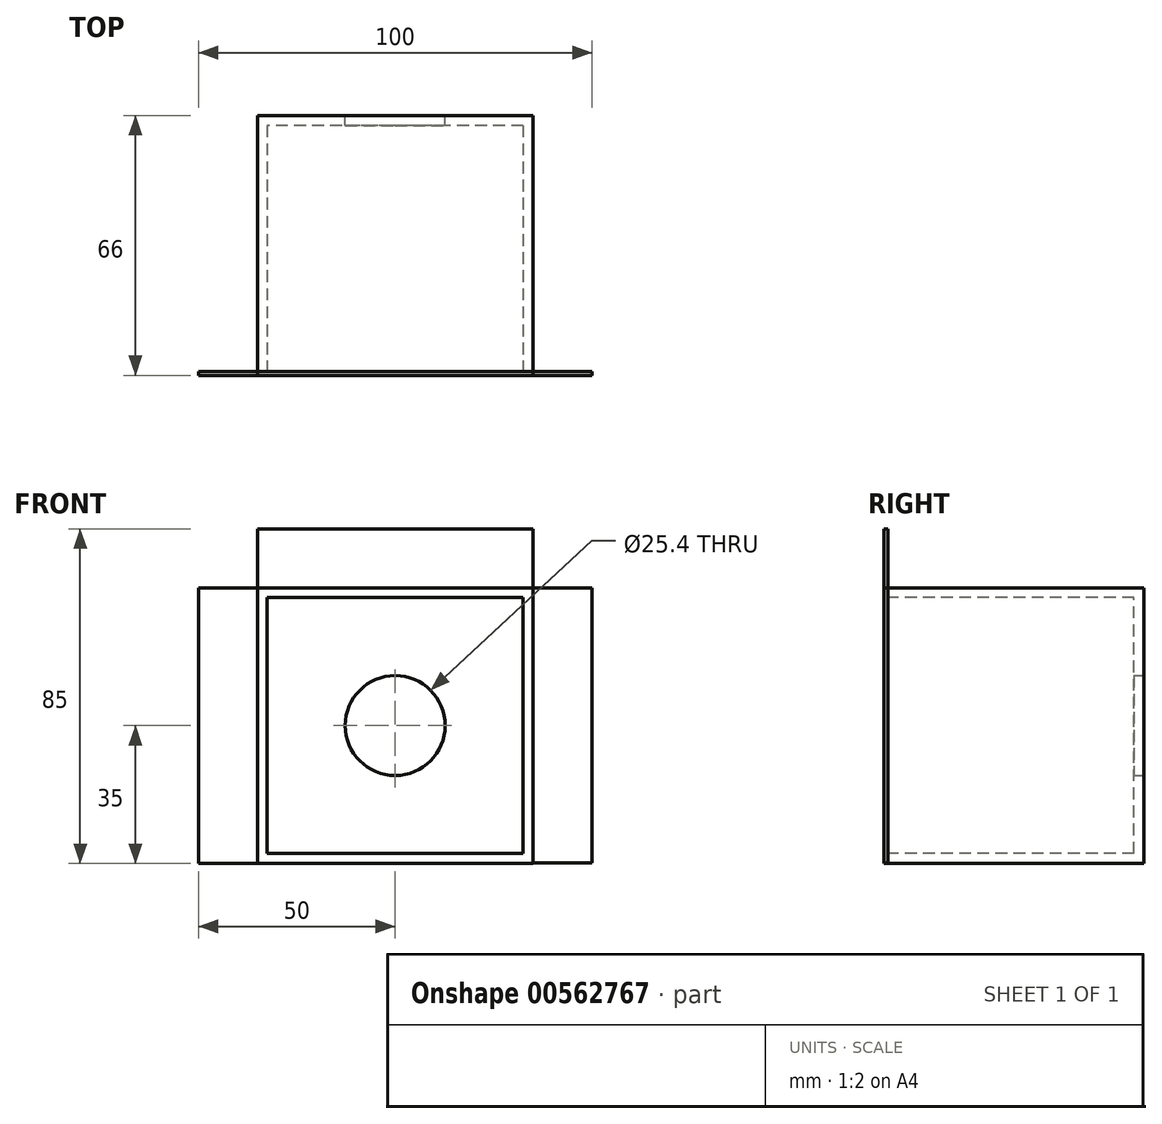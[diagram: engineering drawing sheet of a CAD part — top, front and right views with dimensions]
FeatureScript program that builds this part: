
annotation { "Feature Type Name" : "Feature", "Feature Type Description" : "" }
export const myFeature = defineFeature(function(context is Context, id is Id, definition is map)
    precondition{}
    {
        {
            var Q0;
            Q0=qCreatedBy(makeId("Front.planeOp"),FACE);
            var sketch = newSketch(context, id + "F0", { "sketchPlane" : qUnion([Q0])});
            skLineSegment(sketch, "E0.bottom", {"start": v(35, -35) * mm, "end": v(-35, -35) * mm});
            skLineSegment(sketch, "E0.top", {"start": v(35, 35) * mm, "end": v(-35, 35) * mm});
            skLineSegment(sketch, "E0.left", {"start": v(35, -35) * mm, "end": v(35, 35) * mm});
            skLineSegment(sketch, "E0.right", {"start": v(-35, -35) * mm, "end": v(-35, 35) * mm});
            skPoint(sketch, "E0.middle", {"position": v(0, 0) * mm});
            skLineSegment(sketch, "E1.bottom", {"start": v(35, 35) * mm, "end": v(50, 35) * mm});
            skLineSegment(sketch, "E1.top", {"start": v(35, -34.88) * mm, "end": v(50, -34.88) * mm});
            skLineSegment(sketch, "E1.left", {"start": v(35, 35) * mm, "end": v(35, -34.88) * mm});
            skLineSegment(sketch, "E1.right", {"start": v(50, 35) * mm, "end": v(50, -34.88) * mm});
            skLineSegment(sketch, "E2.top", {"start": v(35, 50) * mm, "end": v(-35, 50) * mm});
            skLineSegment(sketch, "E2.left", {"start": v(35, 35) * mm, "end": v(35, 50) * mm});
            skLineSegment(sketch, "E2.right", {"start": v(-35, 35) * mm, "end": v(-35, 50) * mm});
            skLineSegment(sketch, "E3.bottom", {"start": v(-35, 35) * mm, "end": v(-50, 35) * mm});
            skLineSegment(sketch, "E3.top", {"start": v(-35, -35) * mm, "end": v(-50, -35) * mm});
            skLineSegment(sketch, "E3.left", {"start": v(-35, 35) * mm, "end": v(-35, -35) * mm});
            skLineSegment(sketch, "E3.right", {"start": v(-50, 35) * mm, "end": v(-50, -35) * mm});
            skLineSegment(sketch, "E4.bottom", {"start": v(-35, -35) * mm, "end": v(35, -35) * mm});
            skLineSegment(sketch, "E4.top", {"start": v(-35, -50) * mm, "end": v(35, -50) * mm});
            skLineSegment(sketch, "E4.left", {"start": v(-35, -35) * mm, "end": v(-35, -50) * mm});
            skLineSegment(sketch, "E4.right", {"start": v(35, -35) * mm, "end": v(35, -50) * mm});
            skSolve(sketch);
        }
        {
            var Q0;
            Q0=qCreatedBy(makeId("Front.planeOp"),FACE);
            cPlane(context, id + "F1", {"entities" : qUnion([Q0]), "cplaneType" : CPlaneType.OFFSET, "offset" : 65 * mm, "oppositeDirection" : true, "width" : 150 * mm, "height" : 150 * mm});
        }
        {
            var Q0;
            Q0=qCreatedBy(id+"F1.planeOp",FACE);
            var sketch = newSketch(context, id + "F2", { "sketchPlane" : qUnion([Q0])});
            skLineSegment(sketch, "E5.bottom", {"start": v(35, 35) * mm, "end": v(-35, 35) * mm});
            skLineSegment(sketch, "E5.top", {"start": v(35, -35) * mm, "end": v(-35, -35) * mm});
            skLineSegment(sketch, "E5.left", {"start": v(35, 35) * mm, "end": v(35, -35) * mm});
            skLineSegment(sketch, "E5.right", {"start": v(-35, 35) * mm, "end": v(-35, -35) * mm});
            skPoint(sketch, "E5.middle", {"position": v(0, 0) * mm});
            skSolve(sketch);
        }
        {
            var Q0;
            Q0=makeQuery(id+"F0.imprint","IMPRINT",FACE,{"disambiguationData":[TD([[makeQuery(id+"F0.imprint","IMPRINT",EDGE,{"derivedFrom":sQuery(id+"F0.wireOp",EDGE,"E0.left")}),1.0]])]});
            var Q1;
            Q1=sQuery(id+"F2.wireOp",VERTEX,"E5.middle");
            extrude(context, id + "F3", {"entities" : qUnion([Q0]), "endBound" : BoundingType.UP_TO_VERTEX, "oppositeDirection" : true, "depth" : 25 * mm, "endBoundEntityVertex" : qUnion([Q1]), "offsetDistance" : 25 * mm});
        }
        {
            var Q0;
            Q0=makeQuery(id+"F0.imprint","IMPRINT",FACE,{"disambiguationData":[TD([[makeQuery(id+"F0.imprint","IMPRINT",EDGE,{"derivedFrom":sQuery(id+"F0.wireOp",EDGE,"E3.bottom")}),1.0]])]});
            var Q1;
            Q1=makeQuery(id+"F0.imprint","IMPRINT",FACE,{"disambiguationData":[TD([[makeQuery(id+"F0.imprint","IMPRINT",EDGE,{"derivedFrom":sQuery(id+"F0.wireOp",EDGE,"E0.top")}),-1.0]])]});
            var Q2;
            Q2=makeQuery(id+"F0.imprint","IMPRINT",FACE,{"disambiguationData":[TD([[makeQuery(id+"F0.imprint","IMPRINT",EDGE,{"derivedFrom":sQuery(id+"F0.wireOp",EDGE,"E1.bottom")}),-1.0]])]});
            var Q3;
            Q3=makeQuery(id+"F0.imprint","IMPRINT",FACE,{"disambiguationData":[TD([[makeQuery(id+"F0.imprint","IMPRINT",EDGE,{"derivedFrom":sQuery(id+"F0.wireOp",EDGE,"E4.bottom")}),-1.0]])]});
            extrude(context, id + "F4", {"entities" : qUnion([Q0, Q1, Q2, Q3]), "depth" : 1 * mm, "offsetDistance" : 25 * mm});
        }
        {
            var Q0;
            Q0=makeQuery(id+"F3.opExtrude","CAP_FACE",FACE,{"disambiguationData":[OSD([sQuery(id+"F0.wireOp",EDGE,"E0.left"),sQuery(id+"F0.wireOp",EDGE,"E1.left"),sQuery(id+"F0.wireOp",EDGE,"E0.top"),sQuery(id+"F0.wireOp",EDGE,"E3.left"),sQuery(id+"F0.wireOp",EDGE,"E4.bottom")])],"isStart":true});
            var Q1;
            Q1=makeQuery(id+"F3.opExtrude","SWEPT_BODY",BODY,{"disambiguationData":[OSD([sQuery(id+"F0.wireOp",EDGE,"E0.left"),sQuery(id+"F0.wireOp",EDGE,"E1.left"),sQuery(id+"F0.wireOp",EDGE,"E0.top"),sQuery(id+"F0.wireOp",EDGE,"E3.left"),sQuery(id+"F0.wireOp",EDGE,"E4.bottom")])]});
            shell(context, id + "F5", {"entities" : qUnion([Q0]), "parts" : qUnion([Q1]), "thickness" : 2.5 * mm});
        }
        {
            var Q0;
            Q0=sQuery(id+"F2.wireOp",VERTEX,"E5.middle");
            var Q1;
            Q1=makeQuery(id+"F3.opExtrude","SWEPT_BODY",BODY,{"disambiguationData":[OSD([sQuery(id+"F0.wireOp",EDGE,"E0.left"),sQuery(id+"F0.wireOp",EDGE,"E1.left"),sQuery(id+"F0.wireOp",EDGE,"E0.top"),sQuery(id+"F0.wireOp",EDGE,"E3.left"),sQuery(id+"F0.wireOp",EDGE,"E4.bottom")])]});
            hole(context, id + "F6", {"style" : HoleStyle.SIMPLE, "endStyle" : HoleEndStyle.THROUGH, "oppositeDirection" : true, "holeDiameter" : 25.4 * mm, "majorDiameter" : 5 * mm, "isTappedThrough" : true, "tappedDepth" : 12 * mm, "tapClearance" : 3, "locations" : qUnion([Q0]), "scope" : qUnion([Q1])});
        }
    });
